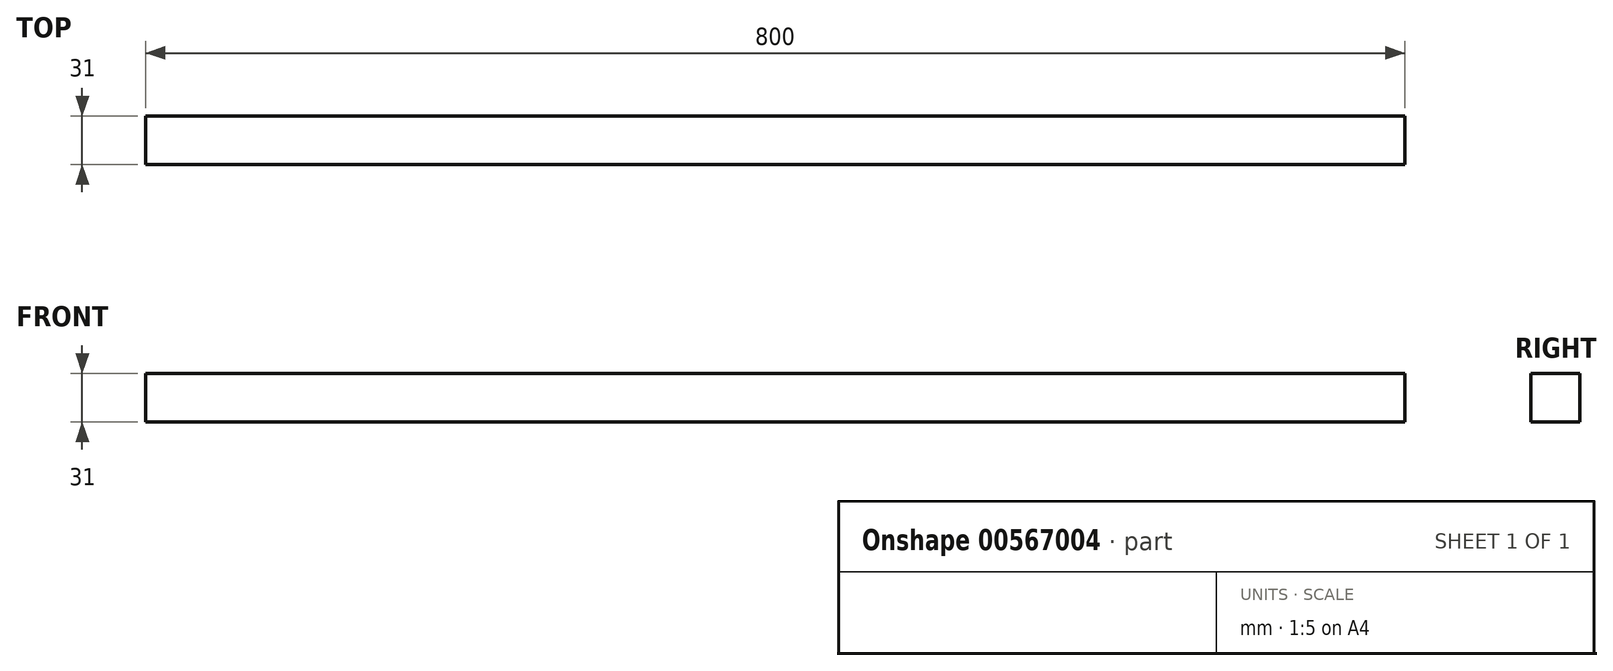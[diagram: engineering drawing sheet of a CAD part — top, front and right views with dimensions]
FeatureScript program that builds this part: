
annotation { "Feature Type Name" : "Feature", "Feature Type Description" : "" }
export const myFeature = defineFeature(function(context is Context, id is Id, definition is map)
    precondition{}
    {
        {
            var Q0;
            Q0=qCreatedBy(makeId("Front.planeOp"),FACE);
            var sketch = newSketch(context, id + "F0", { "sketchPlane" : qUnion([Q0])});
            skLineSegment(sketch, "E0.bottom", {"start": v(-60.8, 70.4) * mm, "end": v(739.2, 70.4) * mm});
            skLineSegment(sketch, "E0.top", {"start": v(-60.8, 39.4) * mm, "end": v(739.2, 39.4) * mm});
            skLineSegment(sketch, "E0.left", {"start": v(-60.8, 70.4) * mm, "end": v(-60.8, 39.4) * mm});
            skLineSegment(sketch, "E0.right", {"start": v(739.2, 70.4) * mm, "end": v(739.2, 39.4) * mm});
            skSolve(sketch);
        }
        {
            var Q0;
            Q0 = qSketchRegion(id + "F0", true);
            extrude(context, id + "F1", {"entities" : qUnion([Q0]), "depth" : 31 * mm, "offsetDistance" : 25 * mm});
        }
    });
